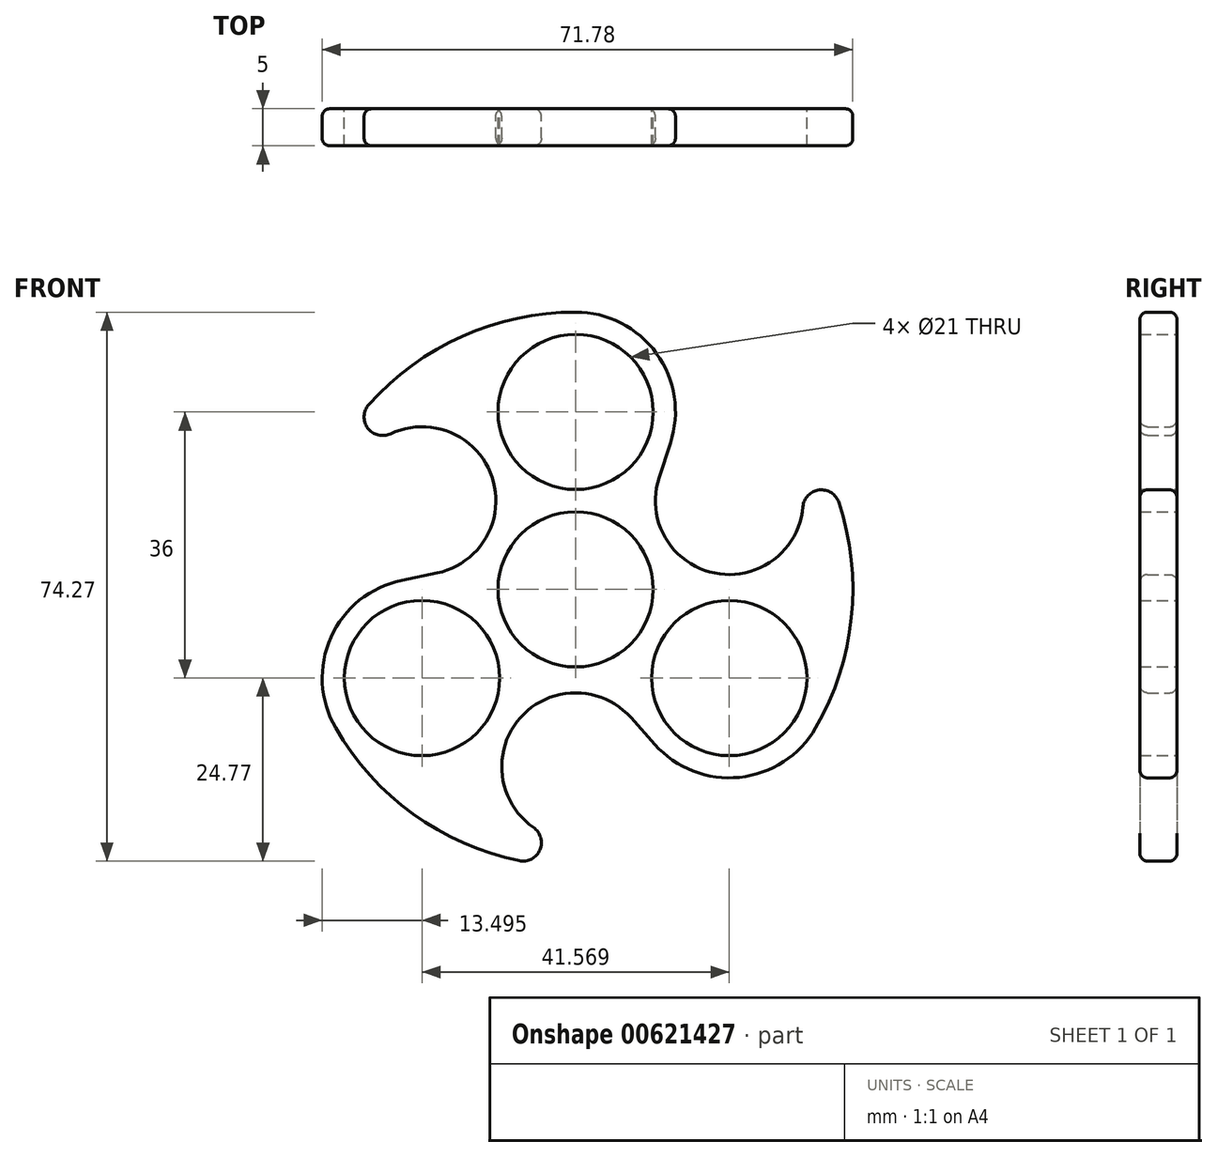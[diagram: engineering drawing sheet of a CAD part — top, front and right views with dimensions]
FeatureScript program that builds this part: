
annotation { "Feature Type Name" : "Feature", "Feature Type Description" : "" }
export const myFeature = defineFeature(function(context is Context, id is Id, definition is map)
    precondition{}
    {
        {
            var Q0;
            Q0=qCreatedBy(makeId("Front.planeOp"),FACE);
            var sketch = newSketch(context, id + "F0", { "sketchPlane" : qUnion([Q0])});
            skArc(sketch, "E0", {"start": v(0, 37.5) * mm, "mid": v(-15.33, 34.23) * mm, "end": v(-27.97, 24.97) * mm});
            skCircle(sketch, "E1", {"center": v(0, 24) * mm, "radius": 10.5 * mm});
            skCircle(sketch, "E2", {"center": v(20.78, -12) * mm, "radius": 10.5 * mm});
            skCircle(sketch, "E3", {"center": v(-20.78, -12) * mm, "radius": 10.5 * mm});
            skCircle(sketch, "E4", {"center": v(0, 0) * mm, "radius": 10.5 * mm});
            skArc(sketch, "E5", {"start": v(12.82, 19.76) * mm, "mid": v(10.94, 31.9) * mm, "end": v(0, 37.5) * mm});
            skArc(sketch, "E6", {"start": v(10.7, -20.98) * mm, "mid": v(22.16, -25.43) * mm, "end": v(32.48, -18.75) * mm});
            skArc(sketch, "E7", {"start": v(-23.53, 1.22) * mm, "mid": v(-33.1, -6.48) * mm, "end": v(-32.48, -18.75) * mm});
            skArc(sketch, "E8", {"start": v(11.29, 15.14) * mm, "mid": v(18.78, 2.2) * mm, "end": v(30.75, 11.16) * mm});
            skArc(sketch, "E9", {"start": v(7.46, -17.35) * mm, "mid": v(-7.49, -17.37) * mm, "end": v(-5.7, -32.21) * mm});
            skArc(sketch, "E10", {"start": v(-18.75, 2.2) * mm, "mid": v(-11.3, 15.17) * mm, "end": v(-25.04, 21.05) * mm});
            skArc(sketch, "E11", {"start": v(-27.97, 24.97) * mm, "mid": v(-28.11, 21.81) * mm, "end": v(-25.04, 21.05) * mm});
            skArc(sketch, "E12", {"start": v(-7.64, -36.71) * mm, "mid": v(-4.84, -35.25) * mm, "end": v(-5.7, -32.21) * mm});
            skLineSegment(sketch, "E13", {"start": v(12.82, 19.76) * mm, "end": v(11.29, 15.14) * mm});
            skLineSegment(sketch, "E14", {"start": v(-23.53, 1.22) * mm, "end": v(-18.75, 2.2) * mm});
            skLineSegment(sketch, "E15", {"start": v(10.7, -20.98) * mm, "end": v(7.46, -17.35) * mm});
            skArc(sketch, "E16.trimOffspring", {"start": v(-32.48, -18.75) * mm, "mid": v(-21.98, -30.38) * mm, "end": v(-7.64, -36.71) * mm});
            skArc(sketch, "E17.trimOffspring", {"start": v(32.48, -18.75) * mm, "mid": v(37.3, -3.84) * mm, "end": v(35.62, 11.74) * mm});
            skLineSegment(sketch, "E18", {"start": v(20.78, 12) * mm, "end": v(-20.78, -12) * mm});
            skLineSegment(sketch, "E19", {"start": v(-20.78, 12) * mm, "end": v(20.78, -12) * mm});
            skLineSegment(sketch, "E20", {"start": v(0, -24) * mm, "end": v(0, 24) * mm});
            skArc(sketch, "E21.converted", {"start": v(35.62, 11.74) * mm, "mid": v(32.95, 13.44) * mm, "end": v(30.75, 11.16) * mm});
            skSolve(sketch);
        }
        {
            var Q0;
            Q0=makeQuery(id+"F0.imprint","IMPRINT",FACE,{"disambiguationData":[TD([[makeQuery(id+"F0.imprint","IMPRINT",EDGE,{"derivedFrom":sQuery(id+"F0.wireOp",EDGE,"E0")}),1.0]])]});
            var Q1;
            Q1=makeQuery(id+"F0.imprint","IMPRINT",FACE,{"disambiguationData":[TD([[makeQuery(id+"F0.imprint","IMPRINT",EDGE,{"derivedFrom":sQuery(id+"F0.wireOp",EDGE,"E3")}),-1.0]])]});
            var Q2;
            Q2=makeQuery(id+"F0.imprint","IMPRINT",FACE,{"disambiguationData":[TD([[makeQuery(id+"F0.imprint","IMPRINT",EDGE,{"derivedFrom":sQuery(id+"F0.wireOp",EDGE,"E2")}),-1.0]])]});
            extrude(context, id + "F1", {"entities" : qUnion([Q0, Q1, Q2]), "depth" : 5 * mm, "offsetDistance" : 25 * mm});
        }
        {
            var Q0;
            Q0=makeQuery(id+"F1.opExtrude","CAP_EDGE",EDGE,{"disambiguationData":[OSD([sQuery(id+"F0.wireOp",EDGE,"E0")])],"isStart":false});
            var Q1;
            Q1=makeQuery(id+"F1.opExtrude","CAP_EDGE",EDGE,{"disambiguationData":[OSD([sQuery(id+"F0.wireOp",EDGE,"E8")])],"isStart":true});
            fillet(context, id + "F2", {"entities" : qUnion([Q0, Q1]), "radius" : 1 * mm, "tangentPropagation" : true, "allowEdgeOverflow" : false});
        }
    });
